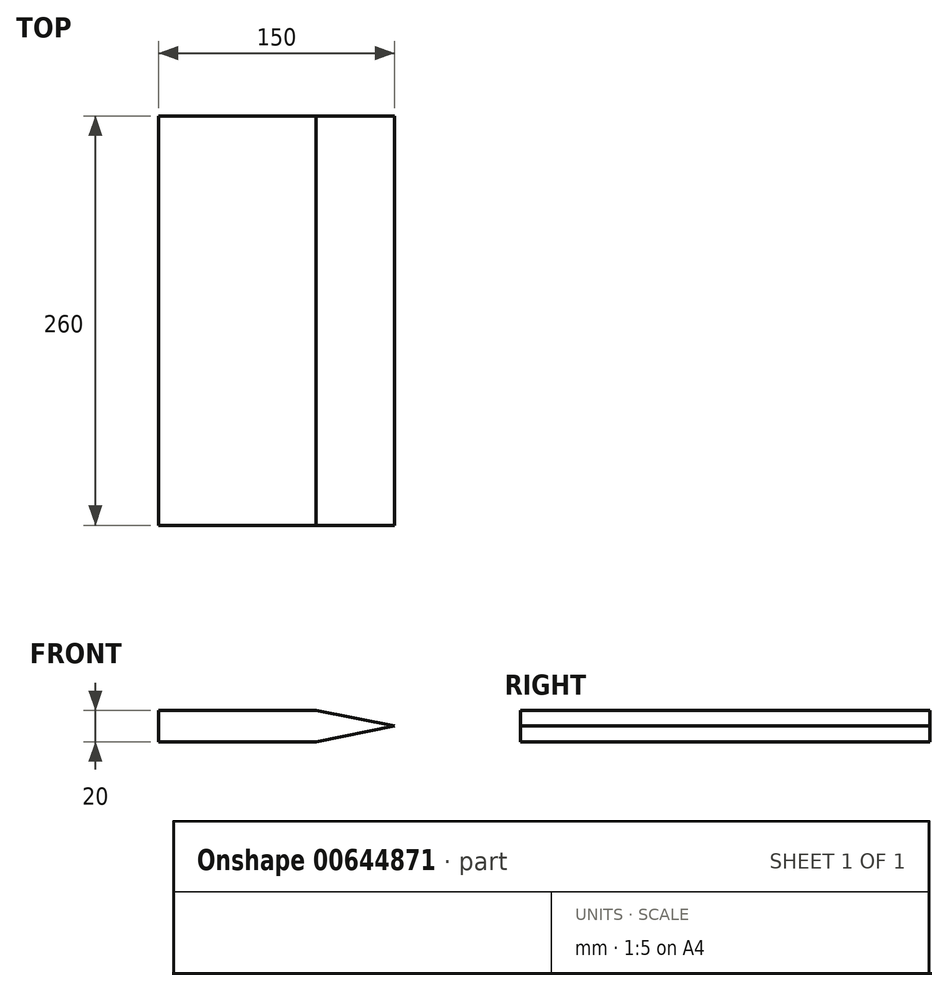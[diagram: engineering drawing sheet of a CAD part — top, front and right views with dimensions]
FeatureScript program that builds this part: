
annotation { "Feature Type Name" : "Feature", "Feature Type Description" : "" }
export const myFeature = defineFeature(function(context is Context, id is Id, definition is map)
    precondition{}
    {
        {
            var Q0;
            Q0=qCreatedBy(makeId("Front.planeOp"),FACE);
            var sketch = newSketch(context, id + "F0", { "sketchPlane" : qUnion([Q0])});
            skLineSegment(sketch, "E0.bottom", {"start": v(0, 0) * mm, "end": v(100, 0) * mm});
            skLineSegment(sketch, "E0.top", {"start": v(0, 20) * mm, "end": v(100, 20) * mm});
            skLineSegment(sketch, "E0.left", {"start": v(0, 0) * mm, "end": v(0, 20) * mm});
            skLineSegment(sketch, "E0.right", {"start": v(100, 0) * mm, "end": v(100, 20) * mm});
            skLineSegment(sketch, "E1", {"start": v(100, 20) * mm, "end": v(150, 10) * mm});
            skLineSegment(sketch, "E2", {"start": v(150, 10) * mm, "end": v(100, 0) * mm});
            skLineSegment(sketch, "E3", {"start": v(100, 10) * mm, "end": v(150, 10) * mm});
            skSolve(sketch);
        }
        {
            var Q0;
            {var subQ1=sQuery(id+"F0.wireOp",EDGE,"E0.bottom");Q0=makeQuery(id+"F0.imprint","IMPRINT",FACE,{"disambiguationData":[TD([[makeQuery(id+"F0.imprint","IMPRINT",EDGE,{"derivedFrom":subQ1}),1.0]])]});}
            var Q1;
            {var subQ0=sQuery(id+"F0.wireOp",EDGE,"E1");Q1=makeQuery(id+"F0.imprint","IMPRINT",FACE,{"disambiguationData":[TD([[makeQuery(id+"F0.imprint","IMPRINT",EDGE,{"derivedFrom":subQ0}),-1.0]])]});}
            var Q2;
            {var subQ0=sQuery(id+"F0.wireOp",EDGE,"E2");Q2=makeQuery(id+"F0.imprint","IMPRINT",FACE,{"disambiguationData":[TD([[makeQuery(id+"F0.imprint","IMPRINT",EDGE,{"derivedFrom":subQ0}),-1.0]])]});}
            extrude(context, id + "F1", {"entities" : qUnion([Q0, Q1, Q2]), "depth" : 260 * mm});
        }
    });
